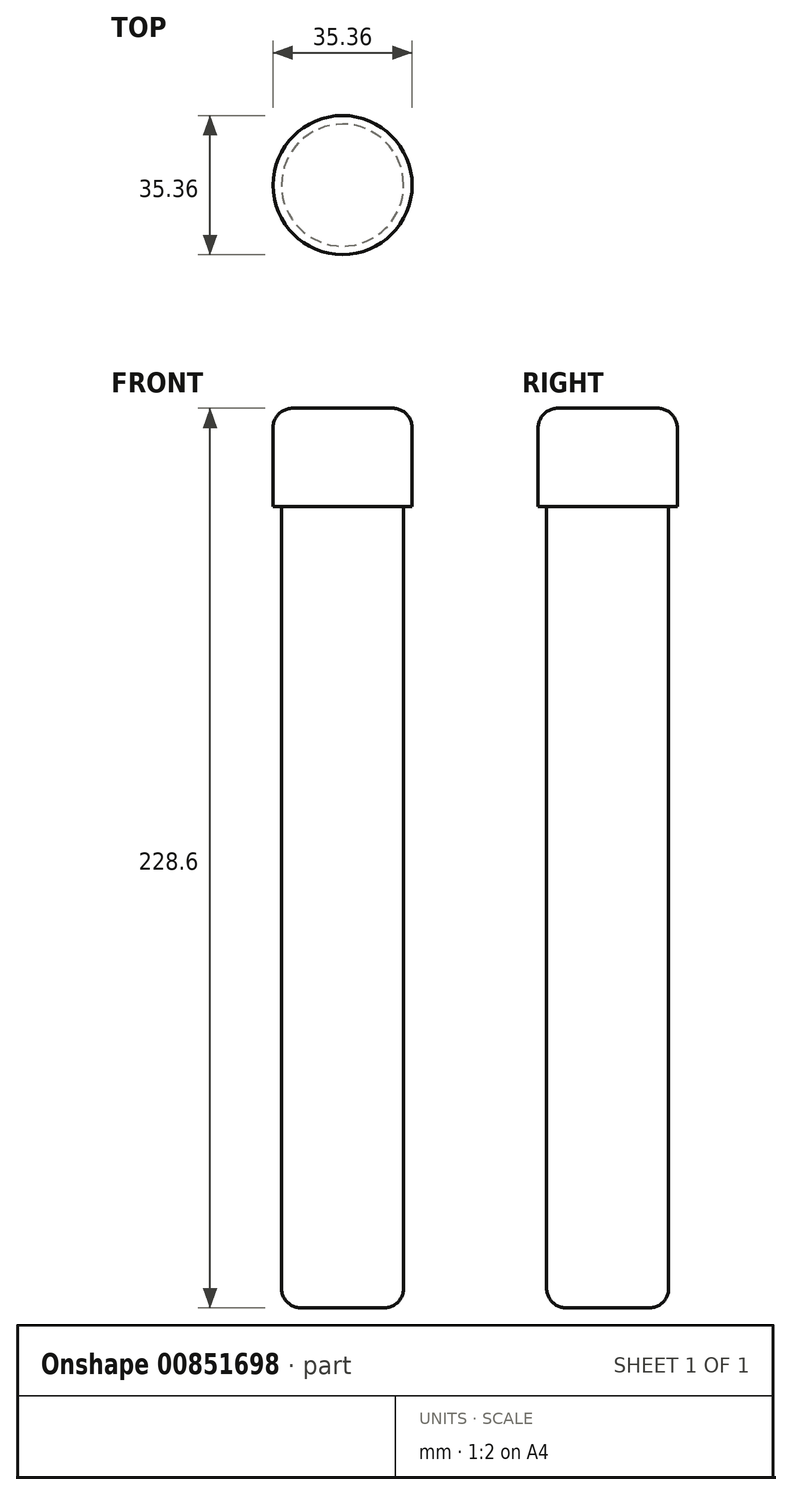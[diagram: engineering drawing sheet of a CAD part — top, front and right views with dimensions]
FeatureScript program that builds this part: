
annotation { "Feature Type Name" : "Feature", "Feature Type Description" : "" }
export const myFeature = defineFeature(function(context is Context, id is Id, definition is map)
    precondition{}
    {
        {
            var Q0;
            Q0=qCreatedBy(makeId("Top.planeOp"),FACE);
            var sketch = newSketch(context, id + "F0", { "sketchPlane" : qUnion([Q0])});
            skCircle(sketch, "E0", {"center": v(0, 0) * mm, "radius": 15.5 * mm});
            skSolve(sketch);
        }
        {
            var Q0;
            Q0=makeQuery(id+"F0.imprint","IMPRINT",FACE,{"disambiguationData":[TD([[makeQuery(id+"F0.imprint","IMPRINT",EDGE,{"derivedFrom":sQuery(id+"F0.wireOp",EDGE,"E0")}),1.0]])]});
            extrude(context, id + "F1", {"entities" : qUnion([Q0]), "depth" : 114.3 * mm, "offsetDistance" : 25 * mm, "hasSecondDirection" : true, "secondDirectionOppositeDirection" : true, "secondDirectionDepth" : 114.3 * mm});
        }
        {
            var Q0;
            Q0=makeQuery(id+"F1.opExtrude","CAP_FACE",FACE,{"disambiguationData":[OSD([sQuery(id+"F0.wireOp",EDGE,"E0")])],"isStart":false});
            var sketch = newSketch(context, id + "F2", { "sketchPlane" : qUnion([Q0])});
            skCircle(sketch, "E1", {"center": v(0, 0) * mm, "radius": 17.68 * mm});
            skSolve(sketch);
        }
        {
            var Q0;
            Q0=makeQuery(id+"F2.imprint","IMPRINT",FACE,{"disambiguationData":[TD([[makeQuery(id+"F2.imprint","IMPRINT",EDGE,{"derivedFrom":sQuery(id+"F2.wireOp",EDGE,"E1")}),1.0]])]});
            var Q1;
            Q1=makeQuery(id+"F2.imprint","IMPRINT",FACE,{"disambiguationData":[TD([[makeQuery(id+"F2.imprint","IMPRINT",EDGE,{"derivedFrom":makeQuery(id+"F1.opExtrude","CAP_EDGE",EDGE,{"disambiguationData":[OSD([sQuery(id+"F0.wireOp",EDGE,"E0")])],"isStart":false})}),1.0]])]});
            extrude(context, id + "F3", {"entities" : qUnion([Q0, Q1]), "operationType" : NewBodyOperationType.ADD, "oppositeDirection" : true, "depth" : 25 * mm, "offsetDistance" : 25 * mm});
        }
        {
            var Q0;
            Q0=makeQuery(id+"F3.boolean.opBoolean","MERGE",FACE,{"derivedFrom":[makeQuery(id+"F1.opExtrude","CAP_FACE",FACE,{"disambiguationData":[OSD([sQuery(id+"F0.wireOp",EDGE,"E0")])],"isStart":false}),makeQuery(id+"F3.opExtrude","CAP_FACE",FACE,{"disambiguationData":[OSD([sQuery(id+"F2.wireOp",EDGE,"E1")])],"isStart":true})]});
            var Q1;
            Q1=makeQuery(id+"FmGmUUdquX9DRjm_1.1.F3.boolean.opBoolean","MERGE",FACE,{"derivedFrom":[makeQuery(id+"F1.opExtrude","CAP_FACE",FACE,{"disambiguationData":[OSD([sQuery(id+"F0.wireOp",EDGE,"E0")])],"isStart":true}),makeQuery(id+"FmGmUUdquX9DRjm_1.1.F3.opExtrude","CAP_FACE",FACE,{"disambiguationData":[OSD([sQuery(id+"F2.wireOp",EDGE,"E1")])],"isStart":true})]});
            fillet(context, id + "F4", {"entities" : qUnion([Q0, Q1]), "radius" : 5 * mm, "tangentPropagation" : true, "allowEdgeOverflow" : false});
        }
    });
